# Revit family: EMABFTL8SC
name_source: partatom
category: Plumbing Fixtures
units: mm (PartAtom-declared; Revit-internal decimal feet)

## family parameters
Always vertical = Yes
Cut with Voids When Loaded = No
OmniClass Number = 23.45.00.00
OmniClass Title = Sanitary, Laundry, and Cleaning Equipment
Part Type = Normal
Room Calculation Point = No
Round Connector Dimension = Use Diameter
Shared = No
Work Plane-Based = No

## types (1)
- EMABFTL8SC
    Activation by = Mechanical Front And Side Bubbler Pushbar
    Approx. Shipping Weight = 94 lbs
    Assembly Code = D2010810
    BUBBLER_MATERIAL = Metal - Steel - Stainless - Chrome
    Bubbler Style = Flexi-Guard ® Safety Bubbler
    CW Connection = Yes
    Chilling Capacity = 8.0 GPH
    DRAIN_MATERIAL = Metal - Steel - Stainless - Chrome
    Description = Elkay Wall Mount Bi-Level ADA Cooler
Non-Filtered Refrigerated Stainless
    Dimensions (L x W x H) = 36-1/4 inch x 18-5/8 inch x 27 inch
    Drain_Pipe 1 1/2" = 1 1/2"
    Finish = Stainless Steel
    Full Load Amps = 5
    HW Connection = No
    Inlet_Pipe = 1/2"
    Installation Location = Indoor
    Manufacturer = Elkay
    Model = EMABFTL8SC
    Mounting Type = Wall Mount (On Wall)
    No. of Stations Served = 2
    Power = 115V/60Hz
    Rated Watts = 370
    SINK_MATERIAL = Metal - Steel - Stainless - Chrome
    Vent Connection = No
    Version = 1.0.0.0
    Waste Connection = Yes

## geometry (parser evidence)
native form markers: Sweep x16
no freeform markers — native parametric forms only
